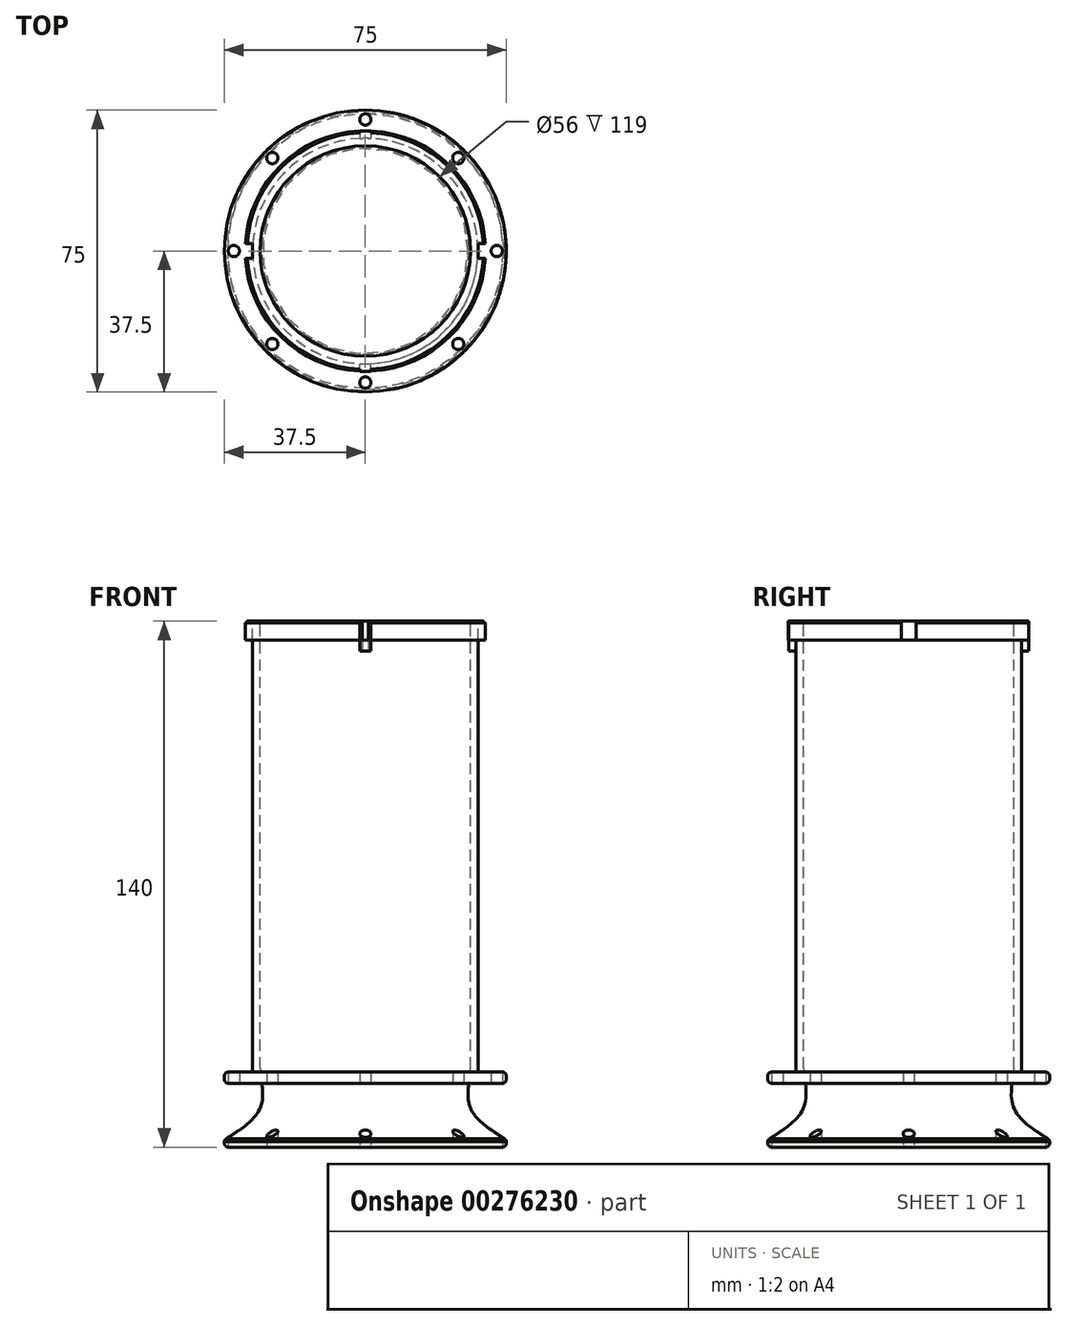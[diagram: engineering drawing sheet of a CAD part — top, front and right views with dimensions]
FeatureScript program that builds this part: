
annotation { "Feature Type Name" : "Feature", "Feature Type Description" : "" }
export const myFeature = defineFeature(function(context is Context, id is Id, definition is map)
    precondition{}
    {
        {
            var Q0;
            Q0=qCreatedBy(makeId("Top.planeOp"),FACE);
            var sketch = newSketch(context, id + "F0", { "sketchPlane" : qUnion([Q0])});
            skCircle(sketch, "E0", {"center": v(0, 0) * mm, "radius": 37.5 * mm});
            skSolve(sketch);
        }
        {
            var Q0;
            Q0=qCreatedBy(makeId("Top.planeOp"),FACE);
            cPlane(context, id + "F1", {"entities" : qUnion([Q0]), "cplaneType" : CPlaneType.OFFSET, "offset" : 10 * mm, "width" : 150 * mm, "height" : 150 * mm});
        }
        {
            var Q0;
            Q0=qCreatedBy(id+"F1.planeOp",FACE);
            var sketch = newSketch(context, id + "F2", { "sketchPlane" : qUnion([Q0])});
            skCircle(sketch, "E1", {"center": v(0, 0) * mm, "radius": 27.5 * mm});
            skSolve(sketch);
        }
        {
            var Q0;
            Q0=qCreatedBy(id+"F1.planeOp",FACE);
            cPlane(context, id + "F3", {"entities" : qUnion([Q0]), "cplaneType" : CPlaneType.OFFSET, "offset" : 5 * mm, "width" : 150 * mm, "height" : 150 * mm});
        }
        {
            var Q0;
            Q0=qCreatedBy(id+"F3.planeOp",FACE);
            var sketch = newSketch(context, id + "F4", { "sketchPlane" : qUnion([Q0])});
            skCircle(sketch, "E2", {"center": v(0, 0) * mm, "radius": 27.5 * mm});
            skSolve(sketch);
        }
        {
            var Q0;
            Q0 = qSketchRegion(id + "F0", true);
            var Q1;
            Q1 = qSketchRegion(id + "F2", true);
            var Q2;
            Q2 = qSketchRegion(id + "F4", true);
            loft(context, id + "F5", {"sheetProfilesArray" : [{ "sheetProfileEntities" : qUnion([Q0]) }, { "sheetProfileEntities" : qUnion([Q1]) }, { "sheetProfileEntities" : qUnion([Q2]) }]});
        }
        {
            var Q0;
            Q0=makeQuery(id+"F5.opLoft","CAP_FACE",FACE,{"disambiguationData":[OSD([makeQuery(id+"F4.imprint","IMPRINT",FACE,{"disambiguationData":[TD([[makeQuery(id+"F4.imprint","IMPRINT",EDGE,{"derivedFrom":sQuery(id+"F4.wireOp",EDGE,"E2")}),1.0]])]})])],"isStart":true});
            var sketch = newSketch(context, id + "F6", { "sketchPlane" : qUnion([Q0])});
            skCircle(sketch, "E3", {"center": v(0, 0) * mm, "radius": 37.5 * mm});
            skSolve(sketch);
        }
        {
            var Q0;
            Q0=qCreatedBy(id+"F3.planeOp",FACE);
            cPlane(context, id + "F7", {"entities" : qUnion([Q0]), "cplaneType" : CPlaneType.OFFSET, "offset" : 3 * mm, "width" : 150 * mm, "height" : 150 * mm});
        }
        {
            var Q0;
            Q0=qCreatedBy(id+"F7.planeOp",FACE);
            var sketch = newSketch(context, id + "F8", { "sketchPlane" : qUnion([Q0])});
            skCircle(sketch, "E4", {"center": v(0, 0) * mm, "radius": 37.5 * mm});
            skSolve(sketch);
        }
        {
            var Q1;
            Q1 = qSketchRegion(id + "F6", true);
            var Q2;
            Q2 = qSketchRegion(id + "F8", true);
            loft(context, id + "F9", {"operationType" : NewBodyOperationType.ADD, "sheetProfilesArray" : [{ "sheetProfileEntities" : qUnion([Q1]) }, { "sheetProfileEntities" : qUnion([Q2]) }]});
        }
        {
            var Q0;
            Q0=makeQuery(id+"F9.opLoft","CAP_FACE",FACE,{"disambiguationData":[OSD([makeQuery(id+"F8.imprint","IMPRINT",FACE,{"disambiguationData":[TD([[makeQuery(id+"F8.imprint","IMPRINT",EDGE,{"derivedFrom":sQuery(id+"F8.wireOp",EDGE,"E4")}),1.0]])]})])],"isStart":true});
            var sketch = newSketch(context, id + "F10", { "sketchPlane" : qUnion([Q0])});
            skCircle(sketch, "E5", {"center": v(0, 0) * mm, "radius": 30 * mm});
            skSolve(sketch);
        }
        {
            var Q0;
            Q0 = qSketchRegion(id + "F10", true);
            extrude(context, id + "F11", {"entities" : qUnion([Q0]), "operationType" : NewBodyOperationType.ADD, "depth" : 120 * mm});
        }
        {
            var Q0;
            Q0=makeQuery(id+"F5.opLoft","CAP_FACE",FACE,{"disambiguationData":[OSD([makeQuery(id+"F0.imprint","IMPRINT",FACE,{"disambiguationData":[TD([[makeQuery(id+"F0.imprint","IMPRINT",EDGE,{"derivedFrom":sQuery(id+"F0.wireOp",EDGE,"E0")}),1.0]])]})])],"isStart":true});
            var sketch = newSketch(context, id + "F12", { "sketchPlane" : qUnion([Q0])});
            skCircle(sketch, "E6", {"center": v(0, 0) * mm, "radius": 37.5 * mm});
            skSolve(sketch);
        }
        {
            var Q0;
            Q0 = qSketchRegion(id + "F12", true);
            extrude(context, id + "F13", {"entities" : qUnion([Q0]), "operationType" : NewBodyOperationType.ADD, "depth" : 2 * mm});
        }
        {
            var Q0;
            Q0=makeQuery(id+"F11.opExtrude","CAP_FACE",FACE,{"disambiguationData":[OSD([sQuery(id+"F10.wireOp",EDGE,"E5")])],"isStart":false});
            var sketch = newSketch(context, id + "F14", { "sketchPlane" : qUnion([Q0])});
            skCircle(sketch, "E7", {"center": v(0, 0) * mm, "radius": 28 * mm});
            skSolve(sketch);
        }
        {
            var Q0;
            Q0 = qSketchRegion(id + "F14", true);
            extrude(context, id + "F15", {"entities" : qUnion([Q0]), "operationType" : NewBodyOperationType.REMOVE, "oppositeDirection" : true, "depth" : 120 * mm});
        }
        {
            var Q0;
            Q0=makeQuery(id+"F11.opExtrude","CAP_FACE",FACE,{"disambiguationData":[OSD([sQuery(id+"F10.wireOp",EDGE,"E5")])],"isStart":false});
            var sketch = newSketch(context, id + "F16", { "sketchPlane" : qUnion([Q0])});
            skCircle(sketch, "E8", {"center": v(0, 0) * mm, "radius": 32 * mm});
            skSolve(sketch);
        }
        {
            var Q0;
            Q0=makeQuery(id+"F16.imprint","IMPRINT",FACE,{"disambiguationData":[TD([[makeQuery(id+"F16.imprint","IMPRINT",EDGE,{"derivedFrom":sQuery(id+"F16.wireOp",EDGE,"E8")}),1.0]])]});
            extrude(context, id + "F17", {"entities" : qUnion([Q0]), "operationType" : NewBodyOperationType.ADD, "oppositeDirection" : true, "depth" : 5 * mm});
        }
        {
            var Q0;
            {var subQ0=sQuery(id+"F10.wireOp",EDGE,"E5");Q0=makeQuery(id+"F17.boolean.opBoolean","MERGE",FACE,{"derivedFrom":[makeQuery(id+"F11.opExtrude","CAP_FACE",FACE,{"disambiguationData":[OSD([subQ0])],"isStart":false}),makeQuery(id+"F17.opExtrude","CAP_FACE",FACE,{"disambiguationData":[OSD([subQ0,sQuery(id+"F16.wireOp",EDGE,"E8")])],"isStart":true})]});}
            var sketch = newSketch(context, id + "F18", { "sketchPlane" : qUnion([Q0])});
            skLineSegment(sketch, "E9.bottom", {"start": v(-32.27, 2) * mm, "end": v(-30.07, 2) * mm});
            skLineSegment(sketch, "E9.top", {"start": v(-32.27, -2) * mm, "end": v(-30.07, -2) * mm});
            skLineSegment(sketch, "E9.left", {"start": v(-32.27, 2) * mm, "end": v(-32.27, -2) * mm});
            skLineSegment(sketch, "E9.right", {"start": v(-30.07, 2) * mm, "end": v(-30.07, -2) * mm});
            skLineSegment(sketch, "E10.MirrorCS", {"start": v(30.07, 2) * mm, "end": v(30.07, -2) * mm});
            skLineSegment(sketch, "E11.MirrorCS", {"start": v(32.27, 2) * mm, "end": v(30.07, 2) * mm});
            skLineSegment(sketch, "E12.MirrorCS", {"start": v(32.27, 2) * mm, "end": v(32.27, -2) * mm});
            skLineSegment(sketch, "E13.MirrorCS", {"start": v(32.27, -2) * mm, "end": v(30.07, -2) * mm});
            skSolve(sketch);
        }
        {
            var Q0;
            Q0 = qSketchRegion(id + "F18", true);
            extrude(context, id + "F19", {"entities" : qUnion([Q0]), "operationType" : NewBodyOperationType.REMOVE, "oppositeDirection" : true, "depth" : 5.8 * mm});
        }
        {
            var Q0;
            {var subQ0=sQuery(id+"F10.wireOp",EDGE,"E5");Q0=makeQuery(id+"F17.boolean.opBoolean","MERGE",FACE,{"derivedFrom":[makeQuery(id+"F11.opExtrude","CAP_FACE",FACE,{"disambiguationData":[OSD([subQ0])],"isStart":false}),makeQuery(id+"F17.opExtrude","CAP_FACE",FACE,{"disambiguationData":[OSD([subQ0,sQuery(id+"F16.wireOp",EDGE,"E8")])],"isStart":true})]});}
            var sketch = newSketch(context, id + "F20", { "sketchPlane" : qUnion([Q0])});
            skLineSegment(sketch, "E14.bottom", {"start": v(-1.5, 31.99) * mm, "end": v(1.5, 31.99) * mm});
            skLineSegment(sketch, "E14.top", {"start": v(-1.5, 29.99) * mm, "end": v(1.5, 29.99) * mm});
            skLineSegment(sketch, "E14.left", {"start": v(-1.5, 31.99) * mm, "end": v(-1.5, 29.99) * mm});
            skLineSegment(sketch, "E14.right", {"start": v(1.5, 31.99) * mm, "end": v(1.5, 29.99) * mm});
            skLineSegment(sketch, "E15.MirrorCS", {"start": v(-1.5, -31.99) * mm, "end": v(1.5, -31.99) * mm});
            skLineSegment(sketch, "E16.MirrorCS", {"start": v(-1.5, -29.99) * mm, "end": v(1.5, -29.99) * mm});
            skLineSegment(sketch, "E17.MirrorCS", {"start": v(1.5, -31.99) * mm, "end": v(1.5, -29.99) * mm});
            skLineSegment(sketch, "E18.MirrorCS", {"start": v(-1.5, -31.99) * mm, "end": v(-1.5, -29.99) * mm});
            skSolve(sketch);
        }
        {
            var Q0;
            Q0 = qSketchRegion(id + "F20", true);
            extrude(context, id + "F21", {"entities" : qUnion([Q0]), "operationType" : NewBodyOperationType.ADD, "oppositeDirection" : true, "depth" : 8 * mm});
        }
        {
            var Q0;
            {var subQ0=makeQuery(id+"F19.opExtrude","SWEPT_FACE",FACE,{"disambiguationData":[OSD([sQuery(id+"F18.wireOp",EDGE,"E11.MirrorCS")])]});var subQ1=sQuery(id+"F16.wireOp",EDGE,"E8");Q0=makeQuery(id+"F21.boolean.opBoolean","SPLIT",EDGE,{"disambiguationData":[TD([makeQuery(id+"F19.boolean.opBoolean","COPY",FACE,{"derivedFrom":subQ0})])],"derivedFrom":makeQuery(id+"F19.boolean.opBoolean","SPLIT",EDGE,{"disambiguationData":[TD([makeQuery(id+"F19.opExtrude","SWEPT_FACE",FACE,{"disambiguationData":[OSD([sQuery(id+"F18.wireOp",EDGE,"E9.bottom")])]})])],"derivedFrom":makeQuery(id+"F17.opExtrude","CAP_EDGE",EDGE,{"disambiguationData":[OSD([subQ1])],"isStart":true})})});}
            var Q1;
            {var subQ0=makeQuery(id+"F19.opExtrude","SWEPT_FACE",FACE,{"disambiguationData":[OSD([sQuery(id+"F18.wireOp",EDGE,"E13.MirrorCS")])]});var subQ2=sQuery(id+"F16.wireOp",EDGE,"E8");Q1=makeQuery(id+"F21.boolean.opBoolean","SPLIT",EDGE,{"disambiguationData":[TD([makeQuery(id+"F19.boolean.opBoolean","COPY",FACE,{"derivedFrom":subQ0})])],"derivedFrom":makeQuery(id+"F19.boolean.opBoolean","SPLIT",EDGE,{"disambiguationData":[TD([makeQuery(id+"F19.opExtrude","SWEPT_FACE",FACE,{"disambiguationData":[OSD([sQuery(id+"F18.wireOp",EDGE,"E9.top")])]})])],"derivedFrom":makeQuery(id+"F17.opExtrude","CAP_EDGE",EDGE,{"disambiguationData":[OSD([subQ2])],"isStart":true})})});}
            var Q2;
            {var subQ0=sQuery(id+"F16.wireOp",EDGE,"E8");var subQ3=makeQuery(id+"F19.opExtrude","SWEPT_FACE",FACE,{"disambiguationData":[OSD([sQuery(id+"F18.wireOp",EDGE,"E9.top")])]});Q2=makeQuery(id+"F21.boolean.opBoolean","SPLIT",EDGE,{"disambiguationData":[TD([makeQuery(id+"F19.boolean.opBoolean","COPY",FACE,{"derivedFrom":subQ3})])],"derivedFrom":makeQuery(id+"F19.boolean.opBoolean","SPLIT",EDGE,{"disambiguationData":[TD([subQ3])],"derivedFrom":makeQuery(id+"F17.opExtrude","CAP_EDGE",EDGE,{"disambiguationData":[OSD([subQ0])],"isStart":true})})});}
            var Q3;
            {var subQ0=sQuery(id+"F16.wireOp",EDGE,"E8");var subQ4=makeQuery(id+"F19.opExtrude","SWEPT_FACE",FACE,{"disambiguationData":[OSD([sQuery(id+"F18.wireOp",EDGE,"E9.bottom")])]});Q3=makeQuery(id+"F21.boolean.opBoolean","SPLIT",EDGE,{"disambiguationData":[TD([makeQuery(id+"F19.boolean.opBoolean","COPY",FACE,{"derivedFrom":subQ4})])],"derivedFrom":makeQuery(id+"F19.boolean.opBoolean","SPLIT",EDGE,{"disambiguationData":[TD([subQ4])],"derivedFrom":makeQuery(id+"F17.opExtrude","CAP_EDGE",EDGE,{"disambiguationData":[OSD([subQ0])],"isStart":true})})});}
            var Q4;
            Q4=makeQuery(id+"F19.boolean.opBoolean","COPY",EDGE,{"derivedFrom":makeQuery(id+"F19.opExtrude","CAP_EDGE",EDGE,{"disambiguationData":[OSD([sQuery(id+"F18.wireOp",EDGE,"E13.MirrorCS")])],"isStart":true})});
            var Q5;
            Q5=makeQuery(id+"F19.boolean.opBoolean","COPY",EDGE,{"derivedFrom":makeQuery(id+"F19.opExtrude","CAP_EDGE",EDGE,{"disambiguationData":[OSD([sQuery(id+"F18.wireOp",EDGE,"E11.MirrorCS")])],"isStart":true})});
            var Q6;
            Q6=makeQuery(id+"F19.boolean.opBoolean","COPY",EDGE,{"derivedFrom":makeQuery(id+"F19.opExtrude","CAP_EDGE",EDGE,{"disambiguationData":[OSD([sQuery(id+"F18.wireOp",EDGE,"E10.MirrorCS")])],"isStart":true})});
            var Q7;
            Q7=makeQuery(id+"F19.boolean.opBoolean","COPY",EDGE,{"derivedFrom":makeQuery(id+"F19.opExtrude","CAP_EDGE",EDGE,{"disambiguationData":[OSD([sQuery(id+"F18.wireOp",EDGE,"E9.top")])],"isStart":true})});
            var Q8;
            Q8=makeQuery(id+"F19.boolean.opBoolean","COPY",EDGE,{"derivedFrom":makeQuery(id+"F19.opExtrude","CAP_EDGE",EDGE,{"disambiguationData":[OSD([sQuery(id+"F18.wireOp",EDGE,"E9.bottom")])],"isStart":true})});
            var Q9;
            Q9=makeQuery(id+"F19.boolean.opBoolean","COPY",EDGE,{"derivedFrom":makeQuery(id+"F19.opExtrude","CAP_EDGE",EDGE,{"disambiguationData":[OSD([sQuery(id+"F18.wireOp",EDGE,"E9.right")])],"isStart":true})});
            chamfer(context, id + "F22", {"entities" : qUnion([Q0, Q1, Q2, Q3, Q4, Q5, Q6, Q7, Q8, Q9]), "width" : .5 * mm, "tangentPropagation" : true});
        }
        {
            var Q0;
            Q0=makeQuery(id+"F15.boolean.opBoolean","COPY",EDGE,{"derivedFrom":makeQuery(id+"F15.opExtrude","CAP_EDGE",EDGE,{"disambiguationData":[OSD([sQuery(id+"F14.wireOp",EDGE,"E7")])],"isStart":true})});
            var Q1;
            Q1=makeQuery(id+"F11.opExtrude","CAP_EDGE",EDGE,{"disambiguationData":[OSD([sQuery(id+"F10.wireOp",EDGE,"E5")])],"isStart":true});
            var Q2;
            Q2=makeQuery(id+"F9.opLoft","MID_CAP_EDGE",EDGE,{"disambiguationData":[OSD([sQuery(id+"F6.wireOp",EDGE,"E3"),sQuery(id+"F8.wireOp",EDGE,"E4")])],"capPos":1.0});
            var Q3;
            Q3=makeQuery(id+"F9.opLoft","MID_CAP_EDGE",EDGE,{"disambiguationData":[OSD([sQuery(id+"F6.wireOp",EDGE,"E3")])],"capPos":0.0});
            var Q4;
            Q4=makeQuery(id+"F5.opLoft","MID_CAP_EDGE",EDGE,{"disambiguationData":[OSD([sQuery(id+"F0.wireOp",EDGE,"E0"),sQuery(id+"F4.wireOp",EDGE,"E2")])],"capPos":2.0});
            var Q5;
            Q5=makeQuery(id+"F13.boolean.opBoolean","MERGE",EDGE,{"derivedFrom":[makeQuery(id+"F5.opLoft","MID_CAP_EDGE",EDGE,{"disambiguationData":[OSD([sQuery(id+"F0.wireOp",EDGE,"E0")])],"capPos":0.0}),makeQuery(id+"F13.opExtrude","CAP_EDGE",EDGE,{"disambiguationData":[OSD([sQuery(id+"F12.wireOp",EDGE,"E6")])],"isStart":true})]});
            var Q6;
            Q6=makeQuery(id+"F13.opExtrude","CAP_EDGE",EDGE,{"disambiguationData":[OSD([sQuery(id+"F12.wireOp",EDGE,"E6")])],"isStart":false});
            var Q7;
            Q7=makeQuery(id+"F15.boolean.opBoolean","COPY",EDGE,{"derivedFrom":makeQuery(id+"F15.opExtrude","CAP_EDGE",EDGE,{"disambiguationData":[OSD([sQuery(id+"F14.wireOp",EDGE,"E7")])],"isStart":false})});
            fillet(context, id + "F23", {"entities" : qUnion([Q0, Q1, Q2, Q3, Q4, Q5, Q6, Q7]), "radius" : 1 * mm, "tangentPropagation" : true, "allowEdgeOverflow" : false});
        }
        {
            var Q0;
            Q0=makeQuery(id+"F13.opExtrude","CAP_FACE",FACE,{"disambiguationData":[OSD([sQuery(id+"F12.wireOp",EDGE,"E6")])],"isStart":false});
            var sketch = newSketch(context, id + "F24", { "sketchPlane" : qUnion([Q0])});
            skLineSegment(sketch, "E19", {"start": v(-34.5, -34.5) * mm, "end": v(41, 41) * mm, "construction": true});
            skLineSegment(sketch, "E20", {"start": v(-42.9, 42.9) * mm, "end": v(53.3, -53.3) * mm, "construction": true});
            skCircle(sketch, "E21", {"center": v(-24.75, 24.75) * mm, "radius": 1.5 * mm});
            skCircle(sketch, "E22", {"center": v(0, 35) * mm, "radius": 1.5 * mm});
            skCircle(sketch, "E23", {"center": v(24.75, 24.75) * mm, "radius": 1.5 * mm});
            skCircle(sketch, "E24.MirrorC", {"center": v(24.75, -24.75) * mm, "radius": 1.5 * mm});
            skCircle(sketch, "E25.MirrorC", {"center": v(-24.75, -24.75) * mm, "radius": 1.5 * mm});
            skCircle(sketch, "E26.MirrorC", {"center": v(0, -35) * mm, "radius": 1.5 * mm});
            skCircle(sketch, "E27", {"center": v(-35, 0) * mm, "radius": 1.5 * mm});
            skCircle(sketch, "E28.MirrorC", {"center": v(35, 0) * mm, "radius": 1.5 * mm});
            skSolve(sketch);
        }
        {
            var Q0;
            Q0 = qSketchRegion(id + "F24", true);
            extrude(context, id + "F25", {"entities" : qUnion([Q0]), "operationType" : NewBodyOperationType.REMOVE, "oppositeDirection" : true, "depth" : 25 * mm});
        }
    });
